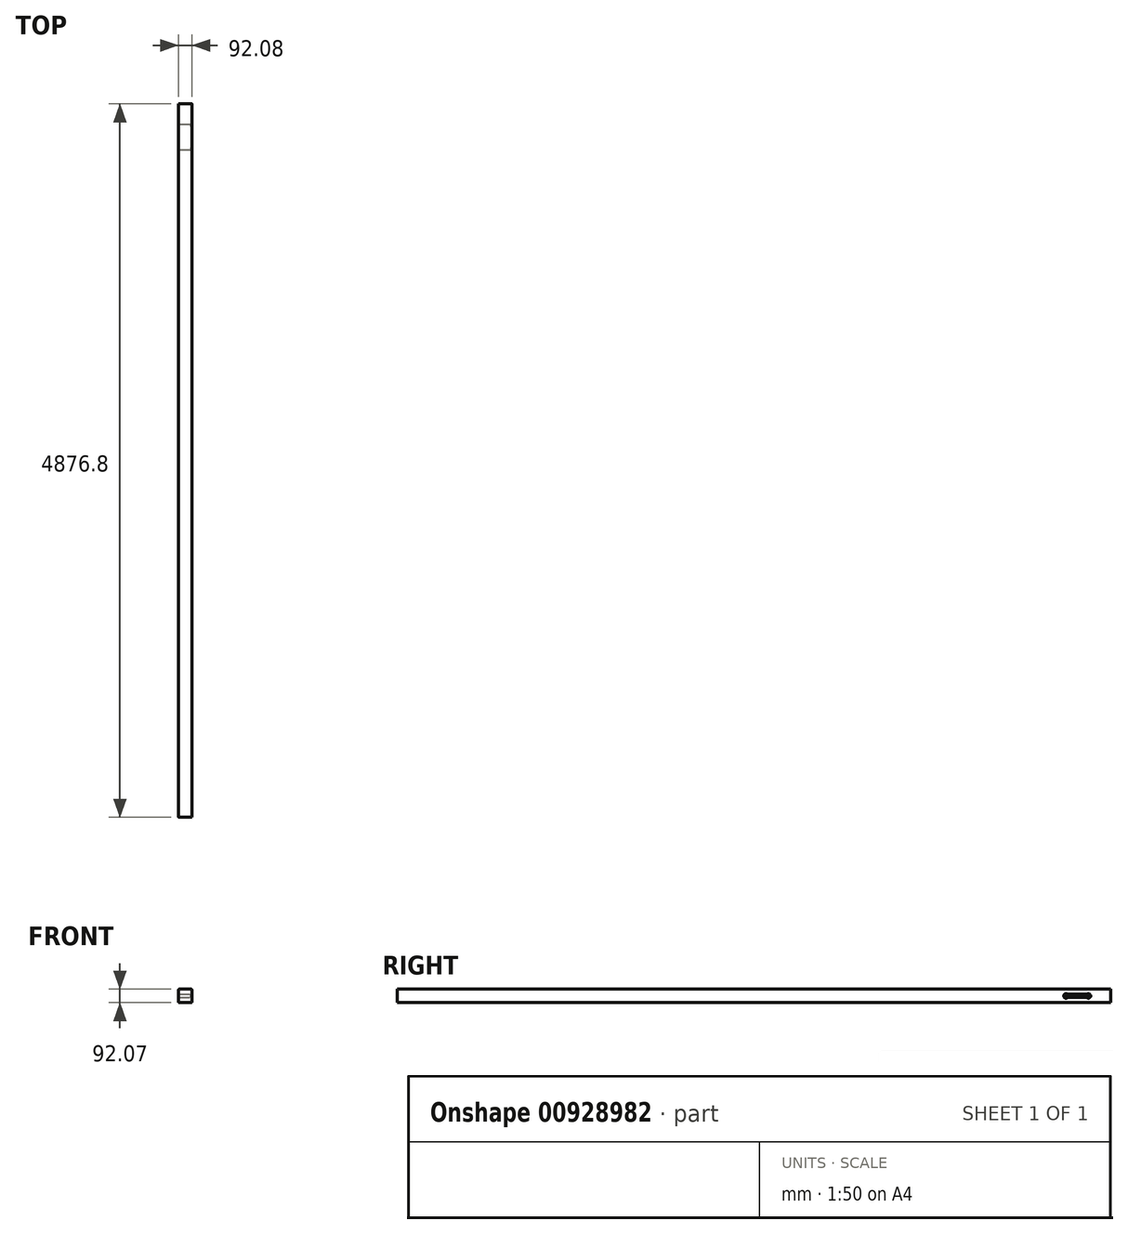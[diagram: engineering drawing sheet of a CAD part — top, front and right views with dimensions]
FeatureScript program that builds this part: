
annotation { "Feature Type Name" : "Feature", "Feature Type Description" : "" }
export const myFeature = defineFeature(function(context is Context, id is Id, definition is map)
    precondition{}
    {
        {
            var Q0;
            Q0=qCreatedBy(makeId("Front.planeOp"),FACE);
            var sketch = newSketch(context, id + "F0", { "sketchPlane" : qUnion([Q0])});
            skLineSegment(sketch, "E0.bottom", {"start": v(-95.2, 62.53) * mm, "end": v(-15.82, 62.53) * mm});
            skLineSegment(sketch, "E0.top", {"start": v(-95.2, -29.54) * mm, "end": v(-15.82, -29.54) * mm});
            skLineSegment(sketch, "E0.left", {"start": v(-101.55, 56.18) * mm, "end": v(-101.55, -23.2) * mm});
            skLineSegment(sketch, "E0.right", {"start": v(-9.47, 56.18) * mm, "end": v(-9.47, -23.2) * mm});
            skPoint(sketch, "E1.visualSharp", {"position": v(-101.55, 62.53) * mm});
            skArc(sketch, "E1.filletArc", {"start": v(-95.2, 62.53) * mm, "mid": v(-99.69, 60.67) * mm, "end": v(-101.55, 56.18) * mm});
            skPoint(sketch, "E2.visualSharp", {"position": v(-9.47, 62.53) * mm});
            skArc(sketch, "E2.filletArc", {"start": v(-9.47, 56.18) * mm, "mid": v(-11.33, 60.67) * mm, "end": v(-15.82, 62.53) * mm});
            skPoint(sketch, "E3.visualSharp", {"position": v(-9.47, -29.54) * mm});
            skArc(sketch, "E3.filletArc", {"start": v(-15.82, -29.54) * mm, "mid": v(-11.33, -27.68) * mm, "end": v(-9.47, -23.2) * mm});
            skPoint(sketch, "E4.visualSharp", {"position": v(-101.55, -29.54) * mm});
            skArc(sketch, "E4.filletArc", {"start": v(-101.55, -23.2) * mm, "mid": v(-99.69, -27.68) * mm, "end": v(-95.2, -29.54) * mm});
            skSolve(sketch);
        }
        {
            var Q0;
            Q0=qSketchRegion(id+"F0",true);
            extrude(context, id + "F1", {"entities" : qUnion([Q0]), "depth" : 4876.8 * mm, "offsetDistance" : 25.4 * mm});
        }
        {
            var Q0;
            Q0=makeQuery(id+"F1.opExtrude","SWEPT_FACE",FACE,{"disambiguationData":[OSD([sQuery(id+"F0.wireOp",EDGE,"E0.right")])]});
            var sketch = newSketch(context, id + "F2", { "sketchPlane" : qUnion([Q0])});
            skPoint(sketch, "E5", {"position": v(-152.4, 16.5) * mm});
            skPoint(sketch, "E6", {"position": v(-304.8, 16.5) * mm});
            skLineSegment(sketch, "E7", {"start": v(-304.8, 56.18) * mm, "end": v(-304.8, -23.2) * mm});
            skLineSegment(sketch, "E8", {"start": v(-152.4, 56.18) * mm, "end": v(-152.4, -23.2) * mm});
            skSolve(sketch);
        }
        {
            var Q0;
            Q0=sQuery(id+"F2.wireOp",VERTEX,"E6");
            var Q1;
            Q1=makeQuery(id+"F1.opExtrude","SWEPT_BODY",BODY,{"disambiguationData":[OSD([sQuery(id+"F0.wireOp",EDGE,"E0.bottom"),sQuery(id+"F0.wireOp",EDGE,"E0.top"),sQuery(id+"F0.wireOp",EDGE,"E0.left"),sQuery(id+"F0.wireOp",EDGE,"E0.right"),sQuery(id+"F0.wireOp",EDGE,"E1.filletArc"),sQuery(id+"F0.wireOp",EDGE,"E2.filletArc"),sQuery(id+"F0.wireOp",EDGE,"E3.filletArc"),sQuery(id+"F0.wireOp",EDGE,"E4.filletArc")])]});
            hole(context, id + "F3", {"style" : HoleStyle.C_SINK, "endStyle" : HoleEndStyle.THROUGH, "holeDiameter" : 22.86 * mm, "cSinkDiameter" : 31.75 * mm, "cSinkAngle" : 82 * degree, "majorDiameter" : 6.35 * mm, "isTappedThrough" : true, "tappedDepth" : 12.7 * mm, "tapClearance" : 3, "locations" : qUnion([Q0]), "scope" : qUnion([Q1]), "startStyle" : HoleStartStyle.SKETCH});
        }
        {
            var Q0;
            Q0=sQuery(id+"F2.wireOp",VERTEX,"E5");
            var Q1;
            Q1=makeQuery(id+"F1.opExtrude","SWEPT_BODY",BODY,{"disambiguationData":[OSD([sQuery(id+"F0.wireOp",EDGE,"E0.bottom"),sQuery(id+"F0.wireOp",EDGE,"E0.top"),sQuery(id+"F0.wireOp",EDGE,"E0.left"),sQuery(id+"F0.wireOp",EDGE,"E0.right"),sQuery(id+"F0.wireOp",EDGE,"E1.filletArc"),sQuery(id+"F0.wireOp",EDGE,"E2.filletArc"),sQuery(id+"F0.wireOp",EDGE,"E3.filletArc"),sQuery(id+"F0.wireOp",EDGE,"E4.filletArc")])]});
            hole(context, id + "F4", {"style" : HoleStyle.C_SINK, "endStyle" : HoleEndStyle.THROUGH, "holeDiameter" : 22.86 * mm, "cSinkDiameter" : 31.75 * mm, "cSinkAngle" : 82 * degree, "majorDiameter" : 6.35 * mm, "isTappedThrough" : true, "tappedDepth" : 12.7 * mm, "tapClearance" : 3, "locations" : qUnion([Q0]), "scope" : qUnion([Q1]), "startStyle" : HoleStartStyle.SKETCH});
        }
        {
            var Q0;
            {var subQ0=sQuery(id+"F2.wireOp",EDGE,"E7");Q0=makeQuery(id+"F2.imprint","IMPRINT",FACE,{"disambiguationData":[TD([[makeQuery(id+"F2.imprint","IMPRINT",EDGE,{"derivedFrom":subQ0}),-1.0]])]});}
            var sketch = newSketch(context, id + "F5", { "sketchPlane" : qUnion([Q0])});
            skLineSegment(sketch, "E9.bottom", {"start": v(-304.8, 27.93) * mm, "end": v(-152.4, 27.93) * mm});
            skLineSegment(sketch, "E9.top", {"start": v(-304.8, 5.07) * mm, "end": v(-152.4, 5.07) * mm});
            skLineSegment(sketch, "E9.left", {"start": v(-304.8, 27.93) * mm, "end": v(-304.8, 5.07) * mm});
            skLineSegment(sketch, "E9.right", {"start": v(-152.4, 27.93) * mm, "end": v(-152.4, 5.07) * mm});
            skSolve(sketch);
        }
        {
            var Q0;
            Q0=qSketchRegion(id+"F5",true);
            extrude(context, id + "F6", {"entities" : qUnion([Q0]), "operationType" : NewBodyOperationType.REMOVE, "oppositeDirection" : true, "depth" : 101.6 * mm, "offsetDistance" : 25.4 * mm});
        }
    });
